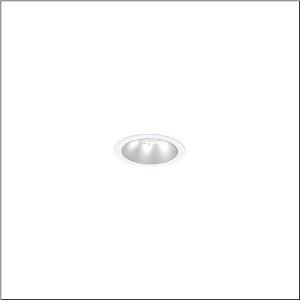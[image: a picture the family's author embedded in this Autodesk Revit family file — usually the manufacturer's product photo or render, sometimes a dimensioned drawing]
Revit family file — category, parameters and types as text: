
# Revit family: lunis_21_s_51db19ea91c
name_source: partatom
category: Lighting Fixtures
units: mm (PartAtom-declared; Revit-internal decimal feet)

## family parameters
Cut with Voids When Loaded = No
Host = Face
Light Source = No
Part Type = Normal
Room Calculation Point = No
Round Connector Dimension = Use Diameter
Shared = No

## types (1)
- --- (1 x LED, 1190 lm, 8 W, 6500K)
    Apparent Load = 8 VA
    CIE Flux Codes = 90 98 100 100 100
    Color Rendering = 80
    Color Temperature = 6500K
    Default Elevation = 1800 mm
    Description = Lunis 21,  S, downlight, light control with lens, of PMMA, anti glare with reflector, of PC, matt, light emission: direct distribution, LED rated luminous flux: 910lm, light colour: 830/840/865, with terminal, 5-pole, mains connection: 220..240V, AC, 50..60Hz, housing, round, of diecast aluminium, traffic white (RAL 9016), diameter: 84mm, clamping range: 1..40mm, protection rating (complete): IP20, protection rating (on room side): IP54, insulation class (complete): insulation class II (safety insulation), certification: CE, impact resistance: IK03, packaging unit: 1 piece
    Height = 0 mm  [stored 0 ft]
    Lamp = 1 x LED
    Lamp Light Flux = 1190 lm
    Lamp Power = 8 W
    Lamp count = 1
    Length = 84 mm
    Luminous efficacy = 149 lm/W
    Manufacturer = Siteco
    ModVariant = No
    Model = 51DB19EA91C
    Mounting Place = Ceiling
    Mounting Type = Recessed
    Number of Poles = 1
    OnlyDefault = Yes
    Power Factor = 1
    Product Name = Lunis 21 S
    Product group = downlight
    ProductGroupID = 400
    Protection Class = Protection class II
    Protection Degree = IP 20
    RLX_Detail_Level = 1
    RLX_Emergency_Light_Flux = 0 lm
    RLX_Emergency_Type = 0
    RLX_Emergency_Type_DB = No
    RlxData = <blob elided: 9613 chars, md5=66f296e5>
    Socket = socket
    Standby Power = 0 W
    System Light Flux = 1190 lm
    System Power = 8 W
    Type Comments = individual setting: colour temperature 6500K, luminous flux: 100 % | (OFF | OFF | ON | OFF) | 200 mA
    Type Image = l_1290846.jpg
    URL = http://relux.com
    VarID = @adj_019184
    Voltage = 0 V
    Weight = 0.00 kg
    Width = 0 mm  [stored 0 ft]

note: [stored X ft] marks values corroborated as IEEE doubles in the binary element streams (Revit-internal decimal feet)

## geometry (parser evidence)
native form markers: Sweep x7
no freeform markers — native parametric forms only
